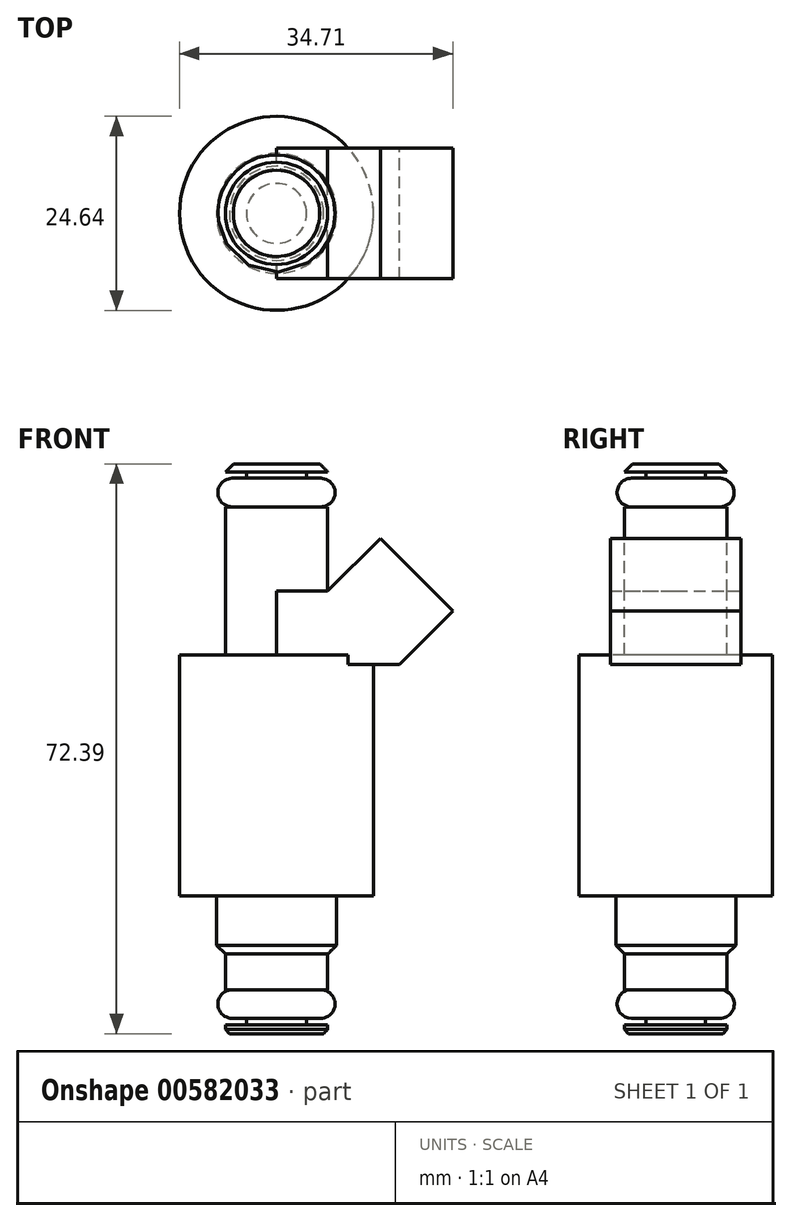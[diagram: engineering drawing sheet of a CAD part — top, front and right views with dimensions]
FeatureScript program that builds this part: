
annotation { "Feature Type Name" : "Feature", "Feature Type Description" : "" }
export const myFeature = defineFeature(function(context is Context, id is Id, definition is map)
    precondition{}
    {
        {
            var Q0;
            Q0=qCreatedBy(makeId("Front.planeOp"),FACE);
            var sketch = newSketch(context, id + "F0", { "sketchPlane" : qUnion([Q0])});
            skPoint(sketch, "E0", {"position": v(0, 72.4) * mm});
            skLineSegment(sketch, "E1", {"start": v(0, 72.4) * mm, "end": v(0, 0) * mm});
            skLineSegment(sketch, "E2", {"start": v(-7.62, 11.23) * mm, "end": v(7.62, 11.23) * mm, "construction": true});
            skPoint(sketch, "E3", {"position": v(0, 11.23) * mm});
            skLineSegment(sketch, "E4", {"start": v(0, 72.4) * mm, "end": v(5.48, 72.4) * mm});
            skLineSegment(sketch, "E5", {"start": v(5.48, 72.4) * mm, "end": v(6.5, 71.37) * mm});
            skLineSegment(sketch, "E6", {"start": v(6.5, 71.37) * mm, "end": v(3.8, 71.37) * mm});
            skLineSegment(sketch, "E7", {"start": v(3.8, 71.37) * mm, "end": v(3.8, 70.56) * mm});
            skLineSegment(sketch, "E8", {"start": v(3.81, 70.56) * mm, "end": v(5.62, 70.56) * mm});
            skArc(sketch, "E9", {"start": v(5.62, 70.56) * mm, "mid": v(7.44, 68.74) * mm, "end": v(5.62, 66.93) * mm});
            skLineSegment(sketch, "E10", {"start": v(5.62, 66.93) * mm, "end": v(6.5, 66.93) * mm});
            skLineSegment(sketch, "E11", {"start": v(6.5, 66.93) * mm, "end": v(6.5, 48.13) * mm});
            skLineSegment(sketch, "E12", {"start": v(6.5, 48.13) * mm, "end": v(6.5, 10.11) * mm, "construction": true});
            skLineSegment(sketch, "E13", {"start": v(6.5, 48.13) * mm, "end": v(12.32, 48.13) * mm});
            skLineSegment(sketch, "E14", {"start": v(12.32, 48.13) * mm, "end": v(12.32, 17.53) * mm});
            skLineSegment(sketch, "E15", {"start": v(12.32, 17.53) * mm, "end": v(7.62, 17.53) * mm});
            skLineSegment(sketch, "E16", {"start": v(7.62, 17.53) * mm, "end": v(7.62, 11.23) * mm});
            skLineSegment(sketch, "E17", {"start": v(7.62, 11.23) * mm, "end": v(6.5, 10.11) * mm});
            skLineSegment(sketch, "E18", {"start": v(6.5, 5.59) * mm, "end": v(6.5, 10.11) * mm});
            skLineSegment(sketch, "E19", {"start": v(6.5, 5.59) * mm, "end": v(5.62, 5.59) * mm});
            skArc(sketch, "E20", {"start": v(5.62, 5.59) * mm, "mid": v(7.44, 3.77) * mm, "end": v(5.63, 1.96) * mm});
            skLineSegment(sketch, "E21", {"start": v(5.63, 1.96) * mm, "end": v(3.81, 1.96) * mm});
            skLineSegment(sketch, "E22", {"start": v(3.81, 1.96) * mm, "end": v(3.81, 1.12) * mm});
            skLineSegment(sketch, "E23", {"start": v(3.81, 1.12) * mm, "end": v(6.5, 1.12) * mm});
            skLineSegment(sketch, "E24", {"start": v(6.5, 1.12) * mm, "end": v(6.5, 0.52) * mm});
            skLineSegment(sketch, "E25", {"start": v(6.5, 0.52) * mm, "end": v(5.98, 0) * mm});
            skLineSegment(sketch, "E26", {"start": v(5.98, 0) * mm, "end": v(0, 0) * mm});
            skLineSegment(sketch, "E27", {"start": v(6.5, 56.22) * mm, "end": v(13.19, 62.91) * mm, "construction": true});
            skLineSegment(sketch, "E28", {"start": v(13.19, 62.91) * mm, "end": v(22.4, 53.7) * mm, "construction": true});
            skLineSegment(sketch, "E29", {"start": v(22.4, 53.7) * mm, "end": v(15.6, 46.92) * mm, "construction": true});
            skLineSegment(sketch, "E30", {"start": v(15.6, 46.92) * mm, "end": v(12.32, 46.92) * mm, "construction": true});
            skArc(sketch, "E31", {"start": v(5.62, 5.59) * mm, "mid": v(3.81, 3.77) * mm, "end": v(5.63, 1.96) * mm, "construction": true});
            skPoint(sketch, "E32", {"position": v(3.81, 3.77) * mm});
            skPoint(sketch, "E33", {"position": v(-6.56, 60.42) * mm});
            skSolve(sketch);
        }
        {
            var Q0;
            Q0=makeQuery(id+"F0.imprint","IMPRINT",FACE,{"disambiguationData":[TD([[makeQuery(id+"F0.imprint","IMPRINT",EDGE,{"derivedFrom":sQuery(id+"F0.wireOp",EDGE,"E1")}),1.0]])]});
            var Q1;
            Q1=sQuery(id+"F0.wireOp",EDGE,"E1");
            revolve(context, id + "F1", {"entities" : qUnion([Q0]), "axis" : qUnion([Q1]), "revolveType" : RevolveType.FULL});
        }
        {
            var Q0;
            Q0=qCreatedBy(makeId("Front.planeOp"),FACE);
            var sketch = newSketch(context, id + "F2", { "sketchPlane" : qUnion([Q0])});
            skLineSegment(sketch, "E34.0", {"start": v(6.5, 56.22) * mm, "end": v(13.19, 62.91) * mm});
            skLineSegment(sketch, "E34.1", {"start": v(13.19, 62.91) * mm, "end": v(22.4, 53.7) * mm});
            skLineSegment(sketch, "E34.2", {"start": v(15.6, 46.92) * mm, "end": v(12.32, 46.92) * mm});
            skLineSegment(sketch, "E34.3", {"start": v(22.4, 53.7) * mm, "end": v(15.6, 46.92) * mm});
            skLineSegment(sketch, "E35", {"start": v(12.32, 46.92) * mm, "end": v(0, 46.92) * mm});
            skLineSegment(sketch, "E36", {"start": v(0, 46.92) * mm, "end": v(0, 56.22) * mm});
            skLineSegment(sketch, "E37", {"start": v(0, 56.22) * mm, "end": v(6.5, 56.22) * mm});
            skSolve(sketch);
        }
        {
            var Q0;
            Q0 = qSketchRegion(id + "F2", true);
            extrude(context, id + "F3", {"entities" : qUnion([Q0]), "operationType" : NewBodyOperationType.ADD, "depth" : 16.6 * mm, "offsetDistance" : 25.4 * mm, "symmetric" : true});
        }
    });
